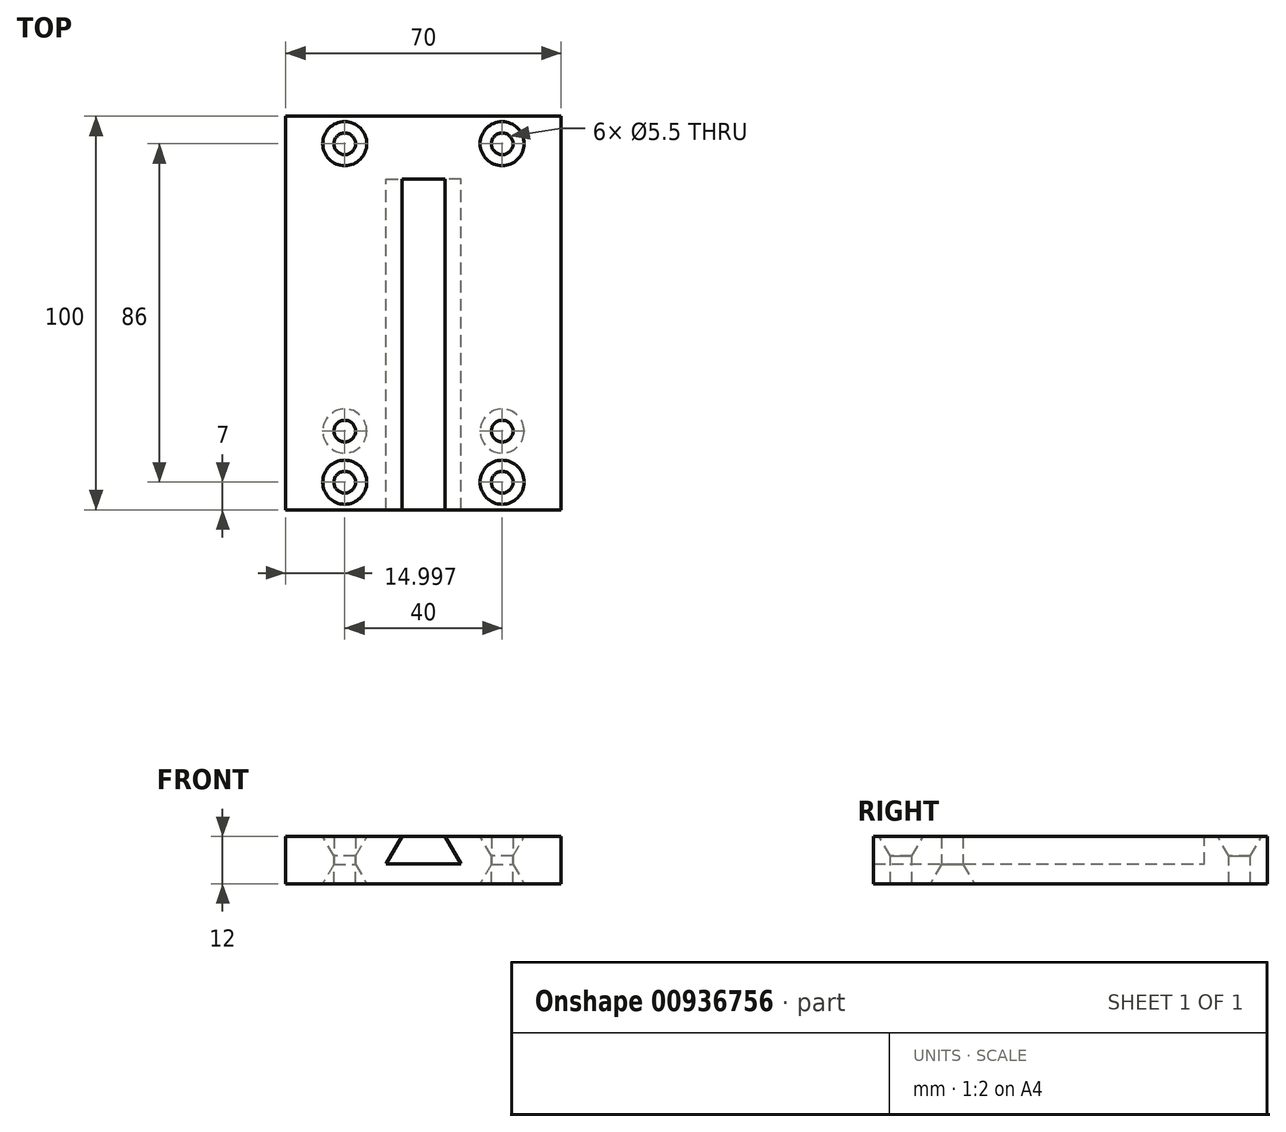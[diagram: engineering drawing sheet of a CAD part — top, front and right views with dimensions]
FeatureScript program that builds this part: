
annotation { "Feature Type Name" : "Feature", "Feature Type Description" : "" }
export const myFeature = defineFeature(function(context is Context, id is Id, definition is map)
    precondition{}
    {
        {
            var Q0;
            Q0=qCreatedBy(makeId("Front.planeOp"),FACE);
            var sketch = newSketch(context, id + "F0", { "sketchPlane" : qUnion([Q0])});
            skLineSegment(sketch, "E0.bottom", {"start": v(-48.1, -12.96) * mm, "end": v(21.9, -12.96) * mm});
            skLineSegment(sketch, "E0.top", {"start": v(-48.1, -0.96) * mm, "end": v(21.9, -0.96) * mm});
            skLineSegment(sketch, "E0.left", {"start": v(-48.1, -12.96) * mm, "end": v(-48.1, -0.96) * mm});
            skLineSegment(sketch, "E0.right", {"start": v(21.9, -12.96) * mm, "end": v(21.9, -0.96) * mm});
            skLineSegment(sketch, "E1", {"start": v(-13.1, -7.96) * mm, "end": v(-22.6, -7.96) * mm});
            skLineSegment(sketch, "E2", {"start": v(-22.6, -7.96) * mm, "end": v(-3.6, -7.96) * mm});
            skLineSegment(sketch, "E3", {"start": v(-22.6, -7.96) * mm, "end": v(-18.55, -0.96) * mm});
            skLineSegment(sketch, "E4", {"start": v(-3.6, -7.96) * mm, "end": v(-7.63, -0.96) * mm});
            skLineSegment(sketch, "E5", {"start": v(-13.1, 3.35) * mm, "end": v(-13.1, -17.02) * mm, "construction": true});
            skPoint(sketch, "E5.startSnap0", {"position": v(-13.1, -0.96) * mm});
            skSolve(sketch);
        }
        {
            var Q0;
            Q0=makeQuery(id+"F0.imprint","IMPRINT",FACE,{"disambiguationData":[TD([[makeQuery(id+"F0.imprint","IMPRINT",EDGE,{"derivedFrom":sQuery(id+"F0.wireOp",EDGE,"E0.bottom")}),1.0]])]});
            extrude(context, id + "F1", {"entities" : qUnion([Q0]), "depth" : 84 * mm, "offsetDistance" : 25 * mm});
        }
        {
            var Q0;
            Q0=makeQuery(id+"F0.imprint","IMPRINT",FACE,{"disambiguationData":[TD([[makeQuery(id+"F0.imprint","IMPRINT",EDGE,{"derivedFrom":sQuery(id+"F0.wireOp",EDGE,"E0.bottom")}),1.0]])]});
            var Q1;
            {var subQ0=sQuery(id+"F0.wireOp",EDGE,"E3");Q1=makeQuery(id+"F0.imprint","IMPRINT",FACE,{"disambiguationData":[TD([[makeQuery(id+"F0.imprint","IMPRINT",EDGE,{"derivedFrom":subQ0}),-1.0]])]});}
            extrude(context, id + "F2", {"entities" : qUnion([Q0, Q1]), "operationType" : NewBodyOperationType.ADD, "depth" : -16 * mm, "offsetDistance" : 25 * mm});
        }
        {
            var Q0;
            {var subQ0=sQuery(id+"F0.wireOp",EDGE,"E0.top");Q0=makeQuery(id+"F2.boolean.opBoolean","MERGE",FACE,{"derivedFrom":[makeQuery(id+"F1.opExtrude","SWEPT_FACE",FACE,{"disambiguationData":[OSD([subQ0]),TDD([makeQuery(id+"F0.imprint","IMPRINT",EDGE,{"disambiguationData":[TD([[makeQuery(id+"F0.imprint","INTERSECT",VERTEX,{"derivedFrom":[subQ0,sQuery(id+"F0.wireOp",EDGE,"E0.left")]}),-1.0]])],"derivedFrom":subQ0})])]}),makeQuery(id+"F1.opExtrude","SWEPT_FACE",FACE,{"disambiguationData":[OSD([subQ0]),TDD([makeQuery(id+"F0.imprint","IMPRINT",EDGE,{"disambiguationData":[TD([[makeQuery(id+"F0.imprint","INTERSECT",VERTEX,{"derivedFrom":[subQ0,sQuery(id+"F0.wireOp",EDGE,"E0.right")]}),1.0]])],"derivedFrom":subQ0})])]}),makeQuery(id+"F2.opExtrude","SWEPT_FACE",FACE,{"disambiguationData":[OSD([subQ0])]})]});}
            var sketch = newSketch(context, id + "F3", { "sketchPlane" : qUnion([Q0])});
            skCircle(sketch, "E6", {"center": v(-33.1, 9) * mm, "radius": 2.5 * mm});
            skCircle(sketch, "E7", {"center": v(6.9, 9) * mm, "radius": 2.5 * mm});
            skCircle(sketch, "E8", {"center": v(-33.1, -77) * mm, "radius": 2.5 * mm});
            skCircle(sketch, "E9", {"center": v(6.9, -77) * mm, "radius": 2.5 * mm});
            skPoint(sketch, "E10.startSnap0", {"position": v(7.14, -84) * mm});
            skCircle(sketch, "E11", {"center": v(6.9, -64) * mm, "radius": 2.5 * mm});
            skCircle(sketch, "E12", {"center": v(-33.1, -64) * mm, "radius": 2.5 * mm});
            skSolve(sketch);
        }
        {
            var Q0;
            Q0=sQuery(id+"F3.wireOp",VERTEX,"E6.center");
            var Q1;
            Q1=sQuery(id+"F3.wireOp",VERTEX,"E7.center");
            var Q2;
            Q2=sQuery(id+"F3.wireOp",VERTEX,"E9.center");
            var Q3;
            Q3=sQuery(id+"F3.wireOp",VERTEX,"E8.center");
            var Q4;
            Q4=makeQuery(id+"F1.opExtrude","SWEPT_BODY",BODY,{"disambiguationData":[OSD([sQuery(id+"F0.wireOp",EDGE,"E0.bottom"),sQuery(id+"F0.wireOp",EDGE,"E0.top"),sQuery(id+"F0.wireOp",EDGE,"E0.left"),sQuery(id+"F0.wireOp",EDGE,"E0.right"),sQuery(id+"F0.wireOp",EDGE,"E2"),sQuery(id+"F0.wireOp",EDGE,"E3"),sQuery(id+"F0.wireOp",EDGE,"E4")])]});
            hole(context, id + "F4", {"style" : HoleStyle.C_SINK, "endStyle" : HoleEndStyle.THROUGH, "holeDiameter" : 5.5 * mm, "cSinkDiameter" : 11.2 * mm, "cSinkAngle" : 60 * degree, "majorDiameter" : 5 * mm, "isTappedThrough" : true, "tappedDepth" : 12 * mm, "tapClearance" : 3, "locations" : qUnion([Q0, Q1, Q2, Q3]), "scope" : qUnion([Q4])});
        }
        {
            var Q0;
            {var subQ0=sQuery(id+"F0.wireOp",EDGE,"E0.bottom");Q0=makeQuery(id+"F2.boolean.opBoolean","MERGE",FACE,{"derivedFrom":[makeQuery(id+"F1.opExtrude","SWEPT_FACE",FACE,{"disambiguationData":[OSD([subQ0])]}),makeQuery(id+"F2.opExtrude","SWEPT_FACE",FACE,{"disambiguationData":[OSD([subQ0])]})]});}
            var sketch = newSketch(context, id + "F5", { "sketchPlane" : qUnion([Q0])});
            skCircle(sketch, "E13", {"center": v(-33.1, 64) * mm, "radius": 2.5 * mm});
            skCircle(sketch, "E14", {"center": v(6.9, 64) * mm, "radius": 2.5 * mm});
            skSolve(sketch);
        }
        {
            var Q0;
            Q0=sQuery(id+"F5.wireOp",VERTEX,"E13.center");
            var Q1;
            Q1=sQuery(id+"F5.wireOp",VERTEX,"E14.center");
            var Q2;
            Q2=makeQuery(id+"F1.opExtrude","SWEPT_BODY",BODY,{"disambiguationData":[OSD([sQuery(id+"F0.wireOp",EDGE,"E0.bottom"),sQuery(id+"F0.wireOp",EDGE,"E0.top"),sQuery(id+"F0.wireOp",EDGE,"E0.left"),sQuery(id+"F0.wireOp",EDGE,"E0.right"),sQuery(id+"F0.wireOp",EDGE,"E2"),sQuery(id+"F0.wireOp",EDGE,"E3"),sQuery(id+"F0.wireOp",EDGE,"E4")])]});
            hole(context, id + "F6", {"style" : HoleStyle.C_SINK, "endStyle" : HoleEndStyle.THROUGH, "holeDiameter" : 5.5 * mm, "cSinkDiameter" : 11.2 * mm, "cSinkAngle" : 60 * degree, "majorDiameter" : 5 * mm, "isTappedThrough" : true, "tappedDepth" : 12 * mm, "tapClearance" : 3, "locations" : qUnion([Q0, Q1]), "scope" : qUnion([Q2])});
        }
    });
